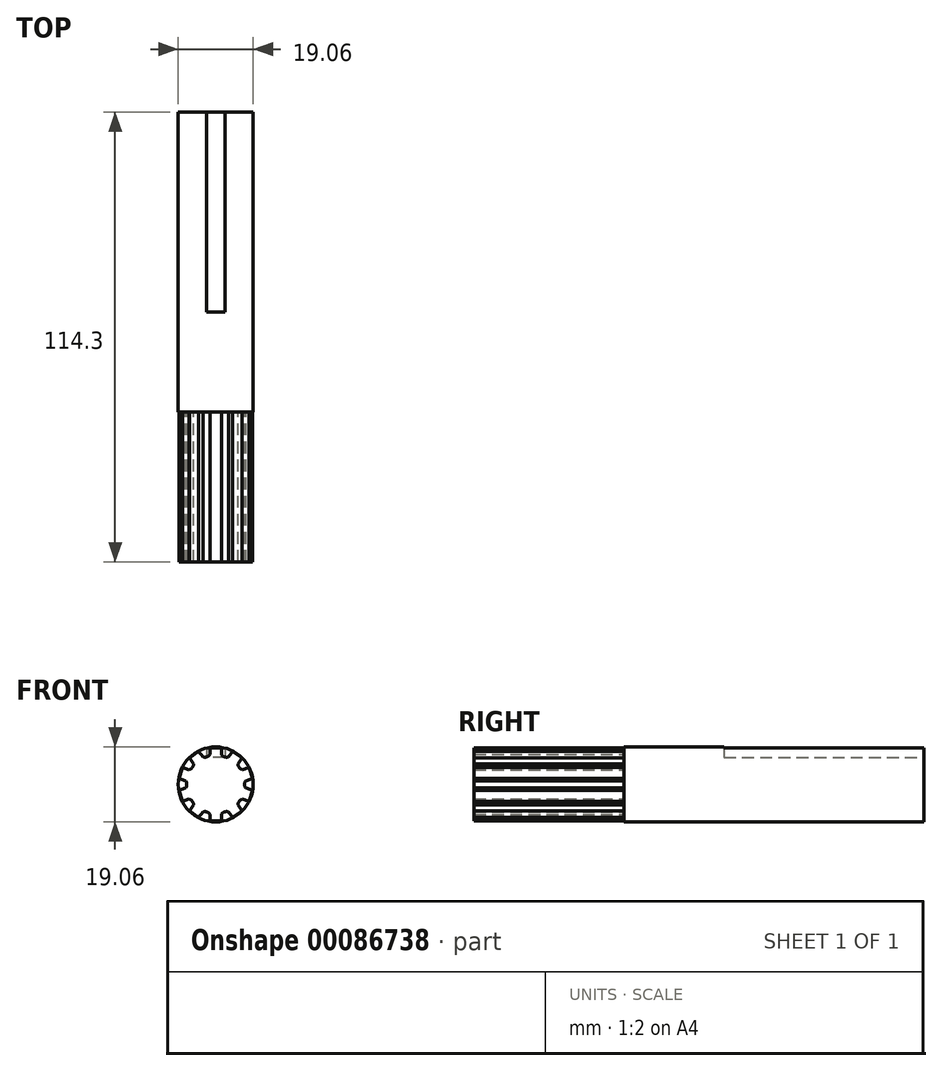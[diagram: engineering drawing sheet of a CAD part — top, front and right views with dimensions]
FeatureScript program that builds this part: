
annotation { "Feature Type Name" : "Feature", "Feature Type Description" : "" }
export const myFeature = defineFeature(function(context is Context, id is Id, definition is map)
    precondition{}
    {
        {
            var Q0;
            Q0=qCreatedBy(makeId("Front.planeOp"),FACE);
            var sketch = newSketch(context, id + "F0", { "sketchPlane" : qUnion([Q0])});
            skLineSegment(sketch, "E0.bottom", {"start": v(1.46, 9.32) * mm, "end": v(-1.46, 9.32) * mm});
            skLineSegment(sketch, "E0.left", {"start": v(1.46, 9.32) * mm, "end": v(1.46, 7.57) * mm});
            skLineSegment(sketch, "E0.right", {"start": v(-1.46, 9.32) * mm, "end": v(-1.46, 7.57) * mm});
            skLineSegment(sketch, "E1.1.0", {"start": v(-4.3, 8.4) * mm, "end": v(-3.27, 6.98) * mm});
            skLineSegment(sketch, "E1.1.1", {"start": v(-4.3, 8.4) * mm, "end": v(-6.66, 6.68) * mm});
            skLineSegment(sketch, "E1.1.2", {"start": v(-6.66, 6.68) * mm, "end": v(-5.63, 5.27) * mm});
            skLineSegment(sketch, "E1.2.0", {"start": v(-8.41, 4.27) * mm, "end": v(-6.75, 3.73) * mm});
            skLineSegment(sketch, "E1.2.1", {"start": v(-8.41, 4.27) * mm, "end": v(-9.32, 1.5) * mm});
            skLineSegment(sketch, "E1.2.2", {"start": v(-9.32, 1.5) * mm, "end": v(-7.65, 0.95) * mm});
            skLineSegment(sketch, "E1.3.0", {"start": v(-9.32, -1.5) * mm, "end": v(-7.65, -0.95) * mm});
            skLineSegment(sketch, "E1.3.1", {"start": v(-9.32, -1.5) * mm, "end": v(-8.41, -4.27) * mm});
            skLineSegment(sketch, "E1.3.2", {"start": v(-8.41, -4.27) * mm, "end": v(-6.75, -3.73) * mm});
            skLineSegment(sketch, "E1.4.0", {"start": v(-6.66, -6.68) * mm, "end": v(-5.63, -5.27) * mm});
            skLineSegment(sketch, "E1.4.1", {"start": v(-6.66, -6.68) * mm, "end": v(-4.3, -8.4) * mm});
            skLineSegment(sketch, "E1.4.2", {"start": v(-4.3, -8.4) * mm, "end": v(-3.27, -6.98) * mm});
            skLineSegment(sketch, "E1.5.0", {"start": v(-1.46, -9.32) * mm, "end": v(-1.46, -7.57) * mm});
            skLineSegment(sketch, "E1.5.1", {"start": v(-1.46, -9.32) * mm, "end": v(1.46, -9.32) * mm});
            skLineSegment(sketch, "E1.5.2", {"start": v(1.46, -9.32) * mm, "end": v(1.46, -7.57) * mm});
            skLineSegment(sketch, "E1.6.0", {"start": v(4.3, -8.4) * mm, "end": v(3.27, -6.98) * mm});
            skLineSegment(sketch, "E1.6.1", {"start": v(4.3, -8.4) * mm, "end": v(6.66, -6.68) * mm});
            skLineSegment(sketch, "E1.6.2", {"start": v(6.66, -6.68) * mm, "end": v(5.63, -5.27) * mm});
            skLineSegment(sketch, "E1.7.0", {"start": v(8.41, -4.27) * mm, "end": v(6.75, -3.73) * mm});
            skLineSegment(sketch, "E1.7.1", {"start": v(8.41, -4.27) * mm, "end": v(9.32, -1.5) * mm});
            skLineSegment(sketch, "E1.7.2", {"start": v(9.32, -1.5) * mm, "end": v(7.65, -0.95) * mm});
            skLineSegment(sketch, "E1.8.0", {"start": v(9.32, 1.5) * mm, "end": v(7.65, 0.95) * mm});
            skLineSegment(sketch, "E1.8.1", {"start": v(9.32, 1.5) * mm, "end": v(8.41, 4.27) * mm});
            skLineSegment(sketch, "E1.8.2", {"start": v(8.41, 4.27) * mm, "end": v(6.75, 3.73) * mm});
            skLineSegment(sketch, "E1.9.0", {"start": v(6.66, 6.68) * mm, "end": v(5.63, 5.27) * mm});
            skLineSegment(sketch, "E1.9.1", {"start": v(6.66, 6.68) * mm, "end": v(4.3, 8.4) * mm});
            skLineSegment(sketch, "E1.9.2", {"start": v(4.3, 8.4) * mm, "end": v(3.27, 6.98) * mm});
            skPoint(sketch, "E1.center", {"position": v(0, 0) * mm});
            skArc(sketch, "E2", {"start": v(5.63, 5.27) * mm, "mid": v(5.94, 4.32) * mm, "end": v(6.75, 3.73) * mm});
            skArc(sketch, "E3.1.0", {"start": v(1.46, 7.57) * mm, "mid": v(2.27, 6.99) * mm, "end": v(3.27, 6.98) * mm});
            skArc(sketch, "E3.2.0", {"start": v(-3.27, 6.98) * mm, "mid": v(-2.27, 6.99) * mm, "end": v(-1.46, 7.57) * mm});
            skArc(sketch, "E3.3.0", {"start": v(-6.75, 3.73) * mm, "mid": v(-5.94, 4.32) * mm, "end": v(-5.63, 5.27) * mm});
            skArc(sketch, "E3.4.0", {"start": v(-7.65, -0.95) * mm, "mid": v(-7.35, 0) * mm, "end": v(-7.65, 0.95) * mm});
            skArc(sketch, "E3.5.0", {"start": v(-5.63, -5.27) * mm, "mid": v(-5.94, -4.32) * mm, "end": v(-6.75, -3.73) * mm});
            skArc(sketch, "E3.6.0", {"start": v(-1.46, -7.57) * mm, "mid": v(-2.27, -6.99) * mm, "end": v(-3.27, -6.98) * mm});
            skArc(sketch, "E3.7.0", {"start": v(3.27, -6.98) * mm, "mid": v(2.27, -6.99) * mm, "end": v(1.46, -7.57) * mm});
            skArc(sketch, "E3.8.0", {"start": v(6.75, -3.73) * mm, "mid": v(5.94, -4.32) * mm, "end": v(5.63, -5.27) * mm});
            skArc(sketch, "E3.9.0", {"start": v(7.65, 0.95) * mm, "mid": v(7.35, 0) * mm, "end": v(7.65, -0.95) * mm});
            skSolve(sketch);
        }
        {
            var Q0;
            Q0=makeQuery(id+"F0.imprint","IMPRINT",FACE,{"disambiguationData":[TD([[makeQuery(id+"F0.imprint","IMPRINT",EDGE,{"derivedFrom":sQuery(id+"F0.wireOp",EDGE,"y5yBF9Nd-YNiM-zbvb-1gcH-5VIxZkdQAmG6")}),1.0]])]});
            var Q1;
            Q1=makeQuery(id+"F0.imprint","IMPRINT",FACE,{"disambiguationData":[TD([[makeQuery(id+"F0.imprint","IMPRINT",EDGE,{"derivedFrom":sQuery(id+"F0.wireOp",EDGE,"E0.bottom")}),1.0]])]});
            extrude(context, id + "F1", {"entities" : qUnion([Q0, Q1]), "depth" : 38.1 * mm});
        }
        {
            var Q0;
            Q0=qCreatedBy(makeId("Front.planeOp"),FACE);
            var sketch = newSketch(context, id + "F2", { "sketchPlane" : qUnion([Q0])});
            skCircle(sketch, "E4", {"center": v(0, 0) * mm, "radius": 9.53 * mm});
            skSolve(sketch);
        }
        {
            var Q0;
            Q0=makeQuery(id+"F2.imprint","IMPRINT",FACE,{"disambiguationData":[TD([[makeQuery(id+"F2.imprint","IMPRINT",EDGE,{"derivedFrom":sQuery(id+"F2.wireOp",EDGE,"E4")}),1.0]])]});
            extrude(context, id + "F3", {"entities" : qUnion([Q0]), "operationType" : NewBodyOperationType.ADD, "oppositeDirection" : true, "depth" : 76.2 * mm});
        }
        {
            var Q0;
            Q0=makeQuery(id+"F3.opExtrude","CAP_FACE",FACE,{"disambiguationData":[OSD([sQuery(id+"F2.wireOp",EDGE,"E4")])],"isStart":false});
            var sketch = newSketch(context, id + "F4", { "sketchPlane" : qUnion([Q0])});
            skLineSegment(sketch, "E5.bottom", {"start": v(-2.38, 9.53) * mm, "end": v(2.38, 9.53) * mm});
            skLineSegment(sketch, "E5.top", {"start": v(-2.38, 6.83) * mm, "end": v(2.38, 6.83) * mm});
            skLineSegment(sketch, "E5.left", {"start": v(-2.38, 9.53) * mm, "end": v(-2.38, 6.83) * mm});
            skLineSegment(sketch, "E5.right", {"start": v(2.38, 9.53) * mm, "end": v(2.38, 6.83) * mm});
            skPoint(sketch, "E5.middle", {"position": v(0, 8.18) * mm});
            skSolve(sketch);
        }
        {
            var Q0;
            {var subQ5=sQuery(id+"F4.wireOp",EDGE,"E5.top");Q0=makeQuery(id+"F4.imprint","IMPRINT",FACE,{"disambiguationData":[TD([[makeQuery(id+"F4.imprint","IMPRINT",EDGE,{"derivedFrom":subQ5}),1.0]])]});}
            extrude(context, id + "F5", {"entities" : qUnion([Q0]), "operationType" : NewBodyOperationType.REMOVE, "oppositeDirection" : true, "depth" : 50.8 * mm});
        }
    });
